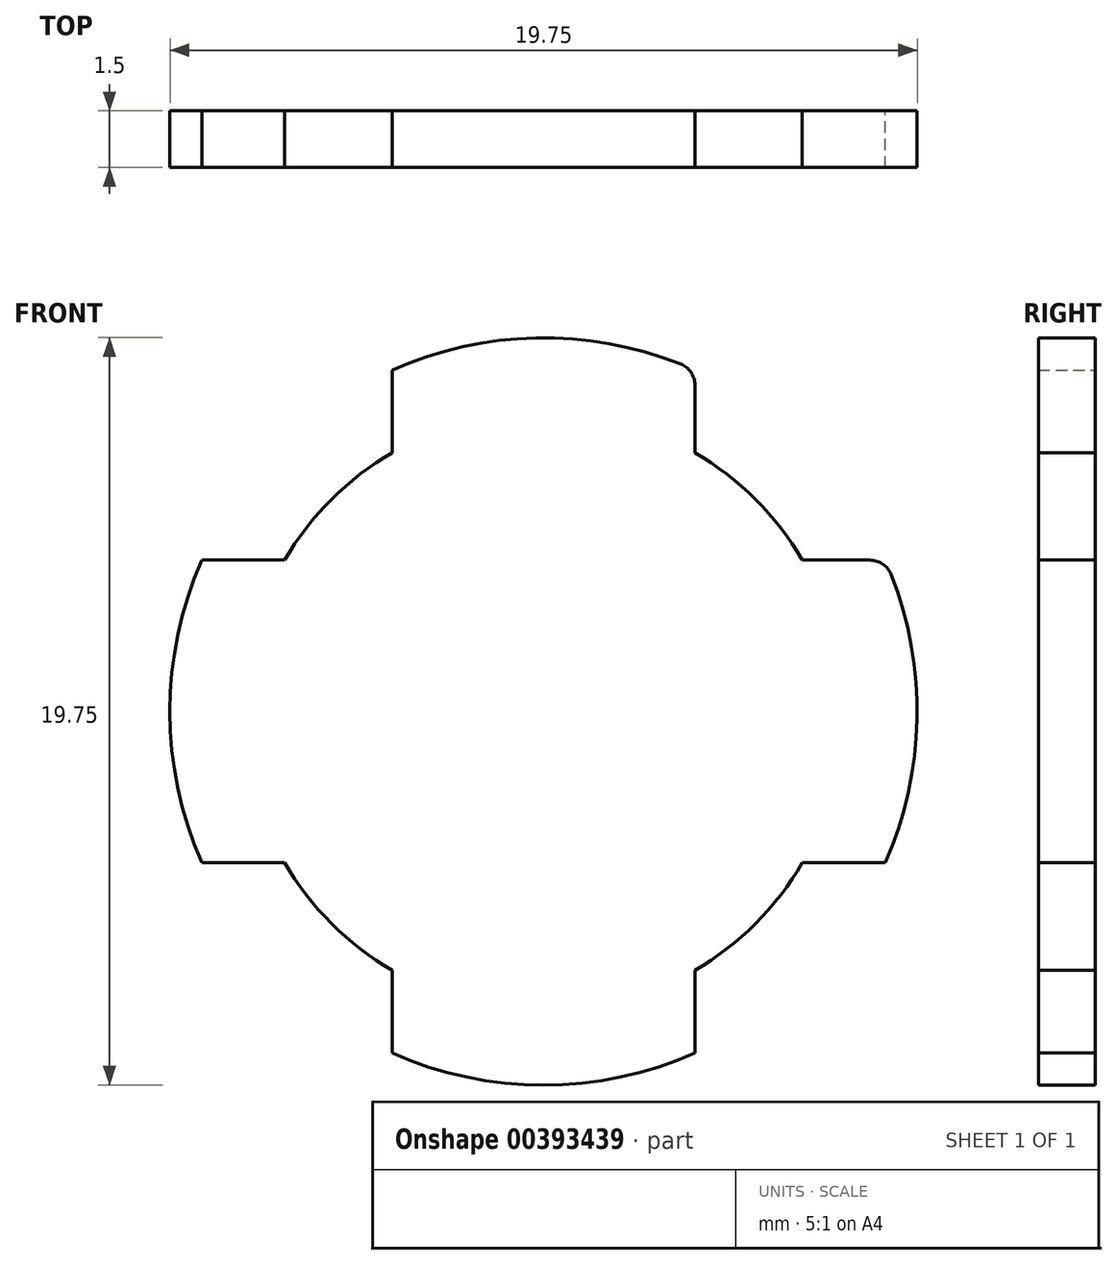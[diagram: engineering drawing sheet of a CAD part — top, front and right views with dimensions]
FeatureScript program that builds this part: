
annotation { "Feature Type Name" : "Feature", "Feature Type Description" : "" }
export const myFeature = defineFeature(function(context is Context, id is Id, definition is map)
    precondition{}
    {
        {
            var Q0;
            Q0=qCreatedBy(makeId("Front.planeOp"),FACE);
            var sketch = newSketch(context, id + "F0", { "sketchPlane" : qUnion([Q0])});
            skCircle(sketch, "E0", {"center": v(0, 0) * mm, "radius": 7.92 * mm});
            skLineSegment(sketch, "E1", {"start": v(4, -6.84) * mm, "end": v(4, -9.03) * mm});
            skLineSegment(sketch, "E2", {"start": v(-4, -6.84) * mm, "end": v(-4, -9.03) * mm});
            skLineSegment(sketch, "E3.1.0", {"start": v(6.84, 4) * mm, "end": v(8.63, 4) * mm});
            skLineSegment(sketch, "E3.2.0", {"start": v(-4, 6.84) * mm, "end": v(-4, 9.03) * mm});
            skLineSegment(sketch, "E3.3.0", {"start": v(-6.84, -4) * mm, "end": v(-9.03, -4) * mm});
            skLineSegment(sketch, "E4.1.0", {"start": v(6.84, -4) * mm, "end": v(9.03, -4) * mm});
            skLineSegment(sketch, "E4.2.0", {"start": v(4, 6.84) * mm, "end": v(4, 8.63) * mm});
            skLineSegment(sketch, "E4.3.0", {"start": v(-6.84, 4) * mm, "end": v(-9.03, 4) * mm});
            skArc(sketch, "E5", {"start": v(9.19, 3.62) * mm, "mid": v(8.97, 3.9) * mm, "end": v(8.63, 4) * mm});
            skArc(sketch, "E6", {"start": v(4, 8.63) * mm, "mid": v(3.9, 8.97) * mm, "end": v(3.62, 9.19) * mm});
            skArc(sketch, "E7.trimOffspring", {"start": v(3.62, 9.19) * mm, "mid": v(-6.98, -6.98) * mm, "end": v(9.19, 3.62) * mm});
            skSolve(sketch);
        }
        {
            var Q0;
            {var subQ0=sQuery(id+"F0.wireOp",EDGE,"E0");var subQ5=makeQuery(id+"F0.imprint","INTERSECT",VERTEX,{"derivedFrom":[subQ0,sQuery(id+"F0.wireOp",EDGE,"E3.1.0")]});Q0=makeQuery(id+"F0.imprint","IMPRINT",FACE,{"disambiguationData":[TD([[makeQuery(id+"F0.imprint","IMPRINT",EDGE,{"disambiguationData":[TD([[subQ5,-1.0]])],"derivedFrom":subQ0}),1.0]])]});}
            var Q1;
            {var subQ0=sQuery(id+"F0.wireOp",EDGE,"E3.3.0");Q1=makeQuery(id+"F0.imprint","IMPRINT",FACE,{"disambiguationData":[TD([[makeQuery(id+"F0.imprint","IMPRINT",EDGE,{"derivedFrom":subQ0}),-1.0]])]});}
            var Q2;
            {var subQ2=sQuery(id+"F0.wireOp",EDGE,"E3.2.0");Q2=makeQuery(id+"F0.imprint","IMPRINT",FACE,{"disambiguationData":[TD([[makeQuery(id+"F0.imprint","IMPRINT",EDGE,{"derivedFrom":subQ2}),-1.0]])]});}
            var Q3;
            {var subQ0=sQuery(id+"F0.wireOp",EDGE,"E1");Q3=makeQuery(id+"F0.imprint","IMPRINT",FACE,{"disambiguationData":[TD([[makeQuery(id+"F0.imprint","IMPRINT",EDGE,{"derivedFrom":subQ0}),-1.0]])]});}
            var Q4;
            {var subQ3=sQuery(id+"F0.wireOp",EDGE,"E3.1.0");Q4=makeQuery(id+"F0.imprint","IMPRINT",FACE,{"disambiguationData":[TD([[makeQuery(id+"F0.imprint","IMPRINT",EDGE,{"derivedFrom":subQ3}),-1.0]])]});}
            extrude(context, id + "F1", {"entities" : qUnion([Q0, Q1, Q2, Q3, Q4]), "depth" : 1.5 * mm});
        }
    });
